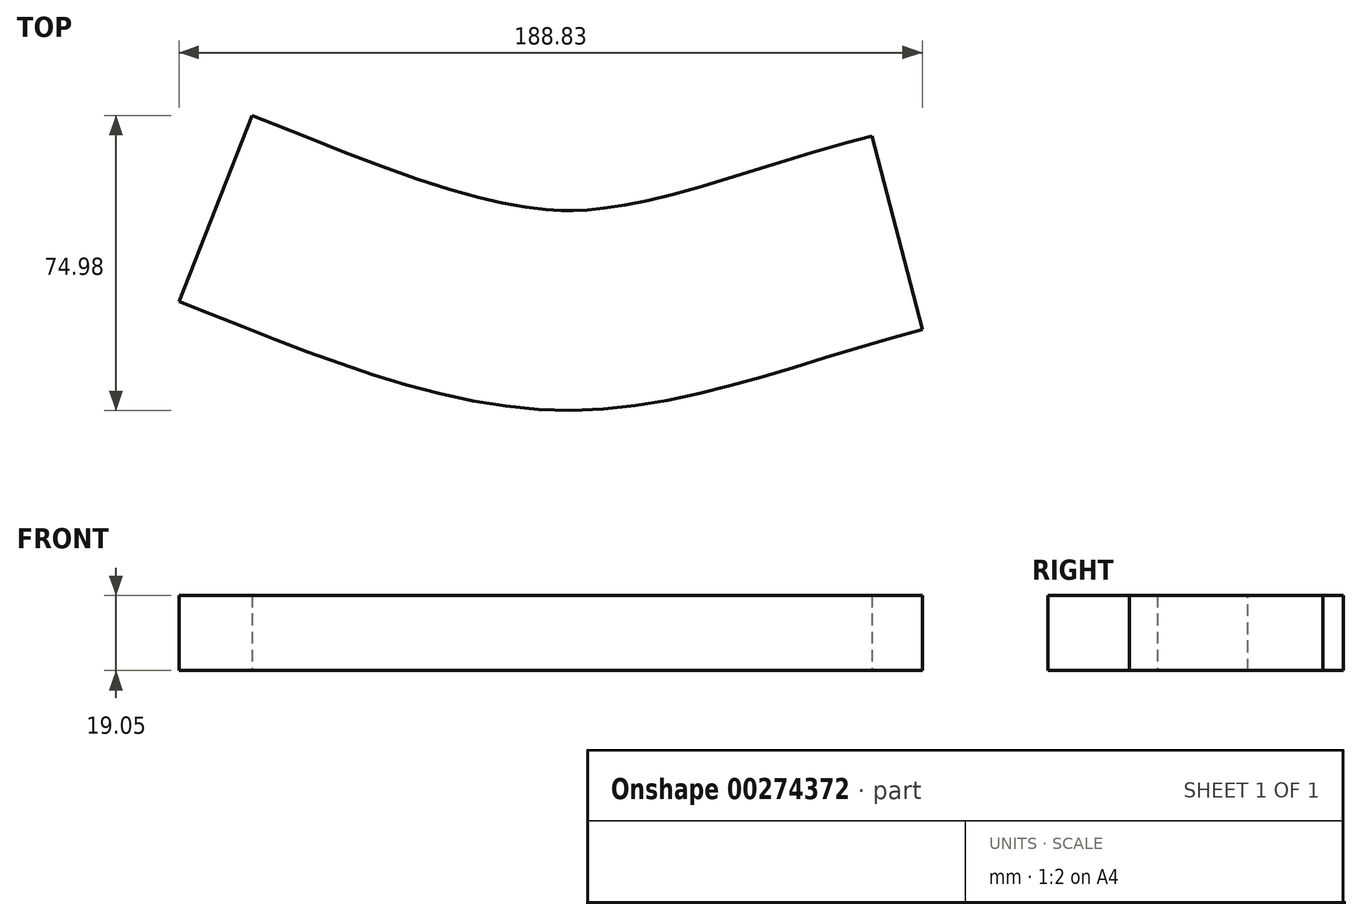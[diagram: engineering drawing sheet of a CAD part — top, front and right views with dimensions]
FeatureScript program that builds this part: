
annotation { "Feature Type Name" : "Feature", "Feature Type Description" : "" }
export const myFeature = defineFeature(function(context is Context, id is Id, definition is map)
    precondition{}
    {
        {
            var Q0;
            Q0=qCreatedBy(makeId("Top.planeOp"),FACE);
            var sketch = newSketch(context, id + "F0", { "sketchPlane" : qUnion([Q0])});
            skFitSpline(sketch, "E0", {"points": [v(-97.33, 27.7) * mm, v(0, 0) * mm, v(91.5, 20.58) * mm], "startDerivative": vector(183.17, -72.03) * mm, "endDerivative": vector(190.51, 49.45) * mm});
            skFitSpline(sketch, "E1.0", {"points": [v(-78.74, 74.97) * mm, v(-74.75, 73.4) * mm, v(-66.9, 70.27) * mm, v(-55.5, 65.74) * mm, v(-44.52, 61.56) * mm, v(-34.05, 57.9) * mm, v(-25.85, 55.4) * mm, v(-19.68, 53.78) * mm, v(-15.26, 52.77) * mm, v(-11.08, 51.96) * mm, v(-7.16, 51.37) * mm, v(-4.12, 51.04) * mm, v(-1.83, 50.88) * mm, v(-0.46, 50.82) * mm, v(0.6, 50.8) * mm, v(1.64, 50.78) * mm, v(2.98, 50.8) * mm, v(4.63, 50.85) * mm, v(6.32, 50.96) * mm, v(8.08, 51.1) * mm, v(10.49, 51.36) * mm, v(13.65, 51.8) * mm, v(17.7, 52.52) * mm, v(21.98, 53.43) * mm, v(26.53, 54.53) * mm, v(32.92, 56.22) * mm, v(41.54, 58.74) * mm, v(52.86, 62.25) * mm, v(65.19, 66.03) * mm, v(74.1, 68.54) * mm, v(78.74, 69.75) * mm]});
            skLineSegment(sketch, "E2", {"start": v(-97.33, 27.7) * mm, "end": v(-78.74, 74.97) * mm});
            skLineSegment(sketch, "E3", {"start": v(78.74, 69.75) * mm, "end": v(91.5, 20.58) * mm});
            skSolve(sketch);
        }
        {
            var Q0;
            Q0 = qSketchRegion(id + "F0", true);
            extrude(context, id + "F1", {"entities" : qUnion([Q0]), "depth" : 19.05 * mm});
        }
    });
